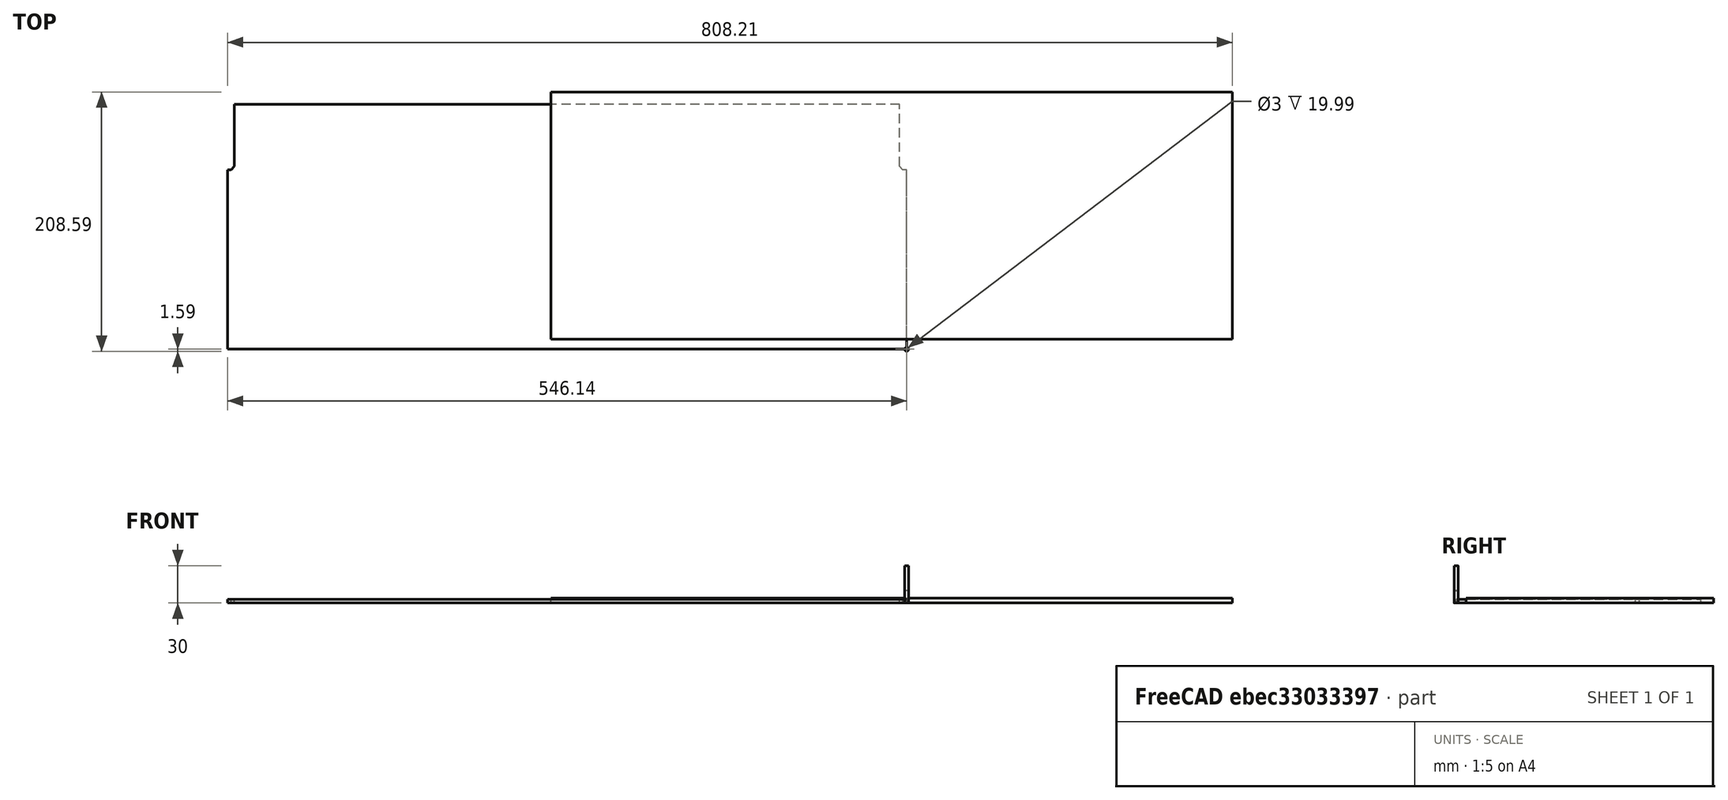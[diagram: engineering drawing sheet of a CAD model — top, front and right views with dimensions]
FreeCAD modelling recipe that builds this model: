
FCSTD DOCUMENT  (FreeCAD 0.22R36731 (Git))
Label: composit_stand9_plexiglass_cut
License: All rights reserved
LicenseURL: http://en.wikipedia.org/wiki/All_rights_reserved
objects: App::DocumentObjectGroup×5, Part::FeaturePython×3, Path::FeaturePython×3, App::Link×1, App::FeaturePython×1
note: 4 computed .brp shape members not serialized (recipe doc carries the construction recipe); baked Part::Feature solids carry a one-line shape summary decoded from their .brp
EXTERNAL_REF file=composit_stand9.FCStd obj=Body024

FEATURE [App::Link] Link  label="Body024"
  LinkedObject = -> <external composit_stand9.FCStd>#Body024
FEATURE [App::DocumentObjectGroup] Group  label="parts"
  Group = -> [Link]
FEATURE [App::FeaturePython] SetupSheet  # Path/CAM operation (typed FeaturePython)
  ClearanceHeightExpression = OpStockZMax+SetupSheet.ClearanceHeightOffset
  ClearanceHeightOffset = 5
  CoolantMode = 0
  CoolantModes = None | Flood | Mist
  FinalDepthExpression = OpFinalDepth
  HorizRapid = 0
  ProfileDirection = 1
  ProfileprocessCircles = true
  ProfileprocessHoles = true
  ProfileprocessPerimeter = true
  SafeHeightExpression = OpStockZMax+SetupSheet.SafeHeightOffset
  SafeHeightOffset = 3
  StartDepthExpression = OpStartDepth
  StepDownExpression = OpToolDiameter
  VertRapid = 0
FEATURE [Part::FeaturePython] Clone  label="Model-Body024"  # Draft clone (typed FeaturePython)
  AttacherType = Attacher::AttachEngine3D
  Fuse = false
  Objects = -> [Link]
  PathResource = Model
  Placement = pos=(-273.071,-9,0) rot=(0,0,1;0rad)
  Scale = (1,1,1)
FEATURE [App::DocumentObjectGroup] Model
  Group = -> [Clone]
FEATURE [Part::FeaturePython] ToolBit  label="3.175mm Endmill"  # Path/CAM toolbit (typed FeaturePython)
  BitPropertyNames = Chipload | CuttingEdgeHeight | Diameter | Flutes | Length | Material | ShankDiameter | SpindleDirection
  BitShape = <path>
  Chipload = 0
  CuttingEdgeHeight = 30
  Diameter = 3.175
  Flutes = 0
  Length = 10
  Material = 0
  ShankDiameter = 3
  ShapeName = endmill
  SpindleDirection = 0
FEATURE [Path::FeaturePython] __175mm_Endmill  label="3.175mm Endmill001"  # Path/CAM operation (typed FeaturePython)
  HorizFeed = 51.6667
  HorizRapid = 0
  SpindleDir = 0
  SpindleSpeed = 18000
  Tool = -> ToolBit
  ToolNumber = 1
  VertFeed = 35
  VertRapid = 0
  expr: HorizRapid = SetupSheet.HorizRapid
  expr: VertRapid = SetupSheet.VertRapid
FEATURE [App::DocumentObjectGroup] Tools
  Group = -> [__175mm_Endmill]
FEATURE [Part::FeaturePython] Stock  # WARN: FeaturePython — macro-defined, semantics opaque (R4)
  Base = -> Model
  ExtXneg = 1
  ExtXpos = 1
  ExtYneg = 1
  ExtYpos = 1
  ExtZneg = 0
  ExtZpos = 1
  Placement = pos=(-285.071,9,0) rot=(0,0,1;0rad)
  StockType = FromBase
FEATURE [Path::FeaturePython] Profile  # Path/CAM operation (typed FeaturePython)
  Active = true
  AreaParams:
    Tolerance = 1e-07
    FitArcs = True
    Simplify = False
    CleanDistance = 0.0
    Accuracy = 0.01
    Unit = 1.0
    MinArcPoints = 4
    MaxArcPoints = 100
    ClipperScale = 10000000.0
    Fill = 0
    Coplanar = 0
    Reorient = True
    Outline = False
    Explode = False
    OpenMode = 0
    Deflection = 0.01
    SubjectFill = 0
    ClipFill = 0
    Offset = 1.5875
    ExtraPass = 0
    Stepover = 0.0
    LastStepover = 0.0
    JoinType = 0
    EndType = 0
    MiterLimit = 2.0
    RoundPrecision = 0.0
    PocketMode = 0
    ToolRadius = 1.0
    PocketExtraOffset = 0.0
    PocketStepover = 0.0
    PocketLastStepover = 0.0
    FromCenter = False
    Angle = 45.0
    AngleShift = 0.0
    Shift = 0.0
    Thicken = False
    SectionCount = -1
    Stepdown = 1.0
    SectionOffset = 0.0
    SectionTolerance = 1e-06
    SectionMode = 2
    Project = False
  ClearanceHeight = 9
  CoolantMode = 0
  CycleTime = 00:00:40
  Direction = 1
  FinalDepth = 0
  HandleMultipleFeatures = 0
  JoinType = 0
  MiterLimit = 0.1
  OffsetExtra = 0
  OpFinalDepth = 0
  OpStartDepth = 4
  OpStockZMax = 4
  OpStockZMin = 0
  OpToolDiameter = 3.175
  PathParams = {'orientation': 0, 'feedrate': 51.666666666666664, 'feedrate_v': 35.0, 'verbose': True, 'resume_height': 7.0, 'retraction': 9.0, 'return_end': True, 'preamble': False, 'start': Vector (-547.0, 0.0, 0.0)}
  SafeHeight = 7
  Side = 0
  SplitArcs = false
  StartDepth = 4
  StartPoint = (-547,0,0)
  StepDown = 10
  ToolController = -> __175mm_Endmill
  UseComp = true
  UseStartPoint = true
  processCircles = true
  processHoles = true
  processPerimeter = true
  expr: ClearanceHeight = OpStockZMax + SetupSheet.ClearanceHeightOffset
  expr: FinalDepth = OpFinalDepth
  expr: SafeHeight = OpStockZMax + SetupSheet.SafeHeightOffset
  expr: StartDepth = OpStartDepth
FEATURE [App::DocumentObjectGroup] Operations
  Group = -> [Profile]
FEATURE [Path::FeaturePython] Job  # Path/CAM operation (typed FeaturePython)
  CycleTime = 00:00:40
  Fixtures = G54
  GeometryTolerance = 0.01
  JobType = 0
  LastPostProcessDate = 2024-04-05 15:18:07.014956
  LastPostProcessOutput = <path>
  Model = -> Model
  Operations = -> Operations
  OrderOutputBy = 2
  PostProcessor = 13
  PostProcessorOutputFile = <path>/%j.tap
  SetupSheet = -> SetupSheet
  SplitOutput = true
  Stock = -> Stock
  Tools = -> Tools
FEATURE [App::DocumentObjectGroup] Group001  label="jobs"
  Group = -> [Job]
note: 3 file-system paths scrubbed to <path> (originals preserved in the JSON sidecar)
